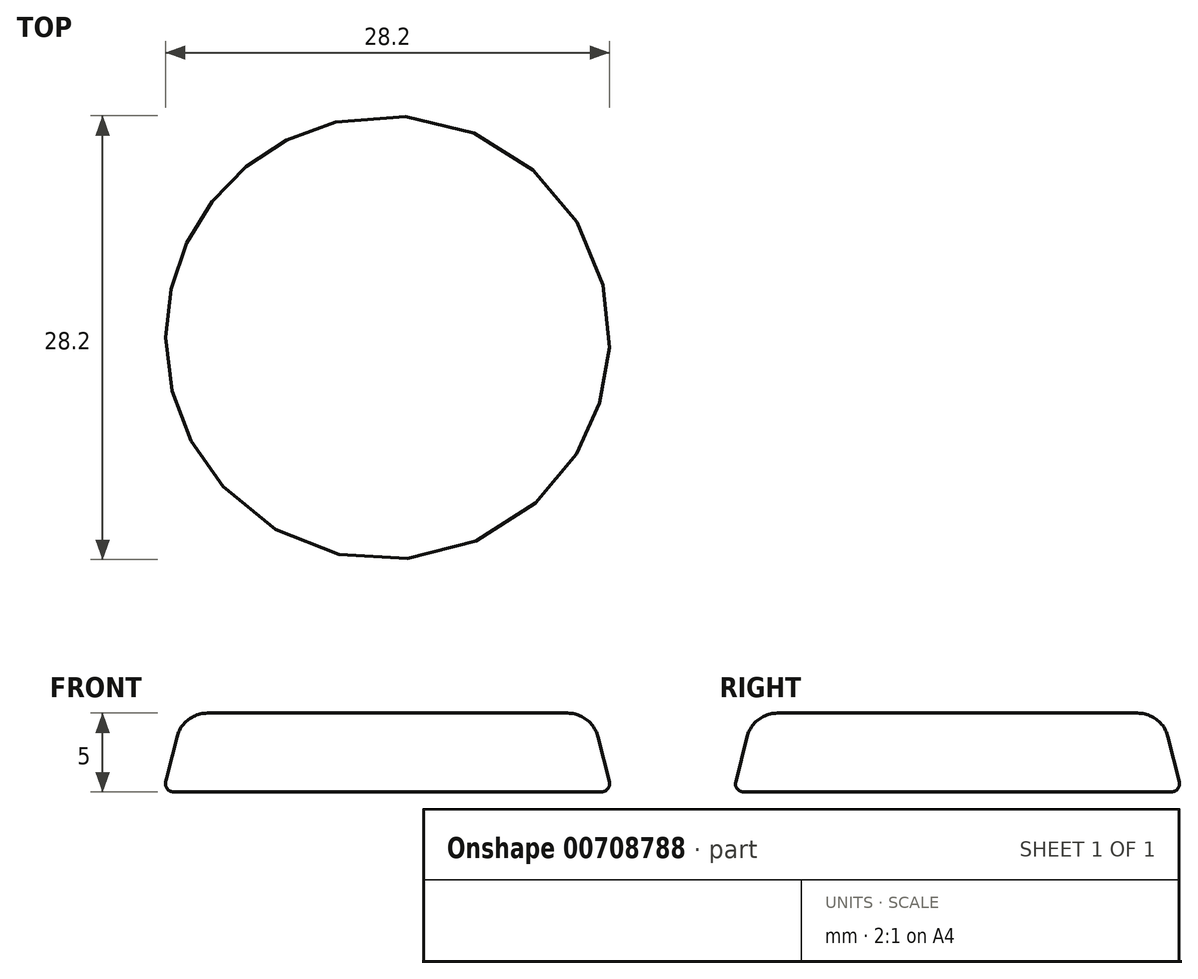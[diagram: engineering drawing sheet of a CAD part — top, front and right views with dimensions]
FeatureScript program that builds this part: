
annotation { "Feature Type Name" : "Feature", "Feature Type Description" : "" }
export const myFeature = defineFeature(function(context is Context, id is Id, definition is map)
    precondition{}
    {
        {
            var Q0;
            Q0=qCreatedBy(makeId("Front.planeOp"),FACE);
            var sketch = newSketch(context, id + "F0", { "sketchPlane" : qUnion([Q0])});
            skLineSegment(sketch, "E0.bottom", {"start": v(0, 0) * mm, "end": v(13, 0) * mm});
            skLineSegment(sketch, "E0.top", {"start": v(0, 5) * mm, "end": v(13, 5) * mm});
            skLineSegment(sketch, "E0.left", {"start": v(0, 0) * mm, "end": v(0, 5) * mm});
            skLineSegment(sketch, "E0.right", {"start": v(13, 0) * mm, "end": v(13, 5) * mm});
            skLineSegment(sketch, "E1", {"start": v(13, 0) * mm, "end": v(14.24, 0) * mm});
            skLineSegment(sketch, "E2", {"start": v(14.24, 0) * mm, "end": v(13, 5) * mm});
            skSolve(sketch);
        }
        {
            var Q0;
            Q0=makeQuery(id+"F0.imprint","IMPRINT",FACE,{"disambiguationData":[TD([[makeQuery(id+"F0.imprint","IMPRINT",EDGE,{"derivedFrom":sQuery(id+"F0.wireOp",EDGE,"E0.bottom")}),1.0]])]});
            var Q1;
            Q1=makeQuery(id+"F0.imprint","IMPRINT",FACE,{"disambiguationData":[TD([[makeQuery(id+"F0.imprint","IMPRINT",EDGE,{"derivedFrom":sQuery(id+"F0.wireOp",EDGE,"E0.right")}),-1.0]])]});
            var Q2;
            Q2=sQuery(id+"F0.wireOp",EDGE,"E0.left");
            revolve(context, id + "F1", {"surfaceOperationType" : NewSurfaceOperationType.NEW, "entities" : qUnion([Q0, Q1]), "axis" : qUnion([Q2]), "revolveType" : RevolveType.FULL});
        }
        {
            var Q0;
            Q0=makeQuery(id+"F1.opRevolve","SWEPT_EDGE",EDGE,{"disambiguationData":[OSD([sQuery(id+"F0.wireOp",EDGE,"E0.top"),sQuery(id+"F0.wireOp",EDGE,"E0.right"),sQuery(id+"F0.wireOp",EDGE,"E2")])]});
            fillet(context, id + "F2", {"entities" : qUnion([Q0]), "radius" : 2 * mm, "tangentPropagation" : true, "allowEdgeOverflow" : false});
        }
        {
            var Q0;
            Q0=makeQuery(id+"F1.opRevolve","SWEPT_EDGE",EDGE,{"disambiguationData":[OSD([sQuery(id+"F0.wireOp",EDGE,"E1"),sQuery(id+"F0.wireOp",EDGE,"E2")])]});
            fillet(context, id + "F3", {"entities" : qUnion([Q0]), "radius" : .5 * mm, "tangentPropagation" : true, "allowEdgeOverflow" : false});
        }
    });
